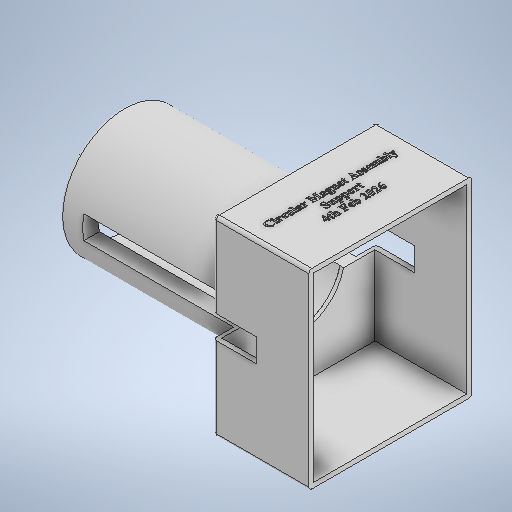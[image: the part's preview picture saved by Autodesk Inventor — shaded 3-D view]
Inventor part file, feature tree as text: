
AUTODESK INVENTOR PART (.ipt)
format: ipt  version: 2025 (Build 290162000, 162)  size: 1,771,008 bytes
history: native  units: in
note: dims shown in document units (in); Inventor stores cm internally (conversion verified against a paired STEP export)
features: sketch x10, extrude x8, fillet x3, emboss x1
ambient origin geometry x8: Origin, YZ Plane, XZ Plane, XY Plane, X Axis, Y Axis, Z Axis, Center Point
bodies: Solid1 (feature_tree)
feature tree (22):
  extrude  "Extrusion1"  Depth=7.0in TaperAngle=0.0deg
  extrude  "Extrusion2"  Depth=7.874in TaperAngle=0.0deg
  extrude  "Extrusion3"  Depth=0.75in TaperAngle=0.0deg
  extrude  "Extrusion4"  Depth=5.2362in
  extrude  "Extrusion5"  Depth=0.1575in
  extrude  "Extrusion7"  Depth=0.1575in TaperAngle=0.0deg
  emboss  "Emboss1"
  extrude  "Extrusion8"  Depth=0.75in
  fillet  "Fillet1"  Radius=7.874in
  fillet  "Fillet2"  Radius=1.378in
  extrude  "Extrusion9"  TaperAngle=0.0deg  [1 undecoded]
  fillet  "Fillet3"  Radius=0.1in
  sketch  "Sketch16"  dims[d32=0.0in d33=0.0in d34=0.1in]
  sketch  "Sketch1"  dims[d0=4.0in d1=7.0in d2=0.0in]
  sketch  "Sketch2"  dims[d3=3.02in d4=7.874in d5=0.0in]
  sketch  "Sketch4"  dims[d6=0.75in d7=5.8155in d8=0.0in]
  sketch  "Sketch5"  dims[d9=6.1417in d10=5.2362in]
  sketch  "Sketch6"  dims[d11=3.0709in d12=0.0in d13=0.1575in]
  sketch  "Sketch10"  dims[d14=0.1575in d15=2.9528in d16=0.0in]
  sketch  "Sketch13"  dims[d19=4.8125in d20=0.0in d21=7.874in d22=0.75in d23=7.874in d24=1.378in d25=0.0in]
  sketch  "Sketch14"  dims[d26=0.0787in d27=0.0in d28=0.0in d29=0.0in d30=0.1in]
  sketch  "Sketch15"  dims[d31=0.1in]
note: 1 required parameter value undecoded (feature->parameter linkage not recoverable at this tier; creation-order binding heuristic only, values carry confidence <= 0.55)
